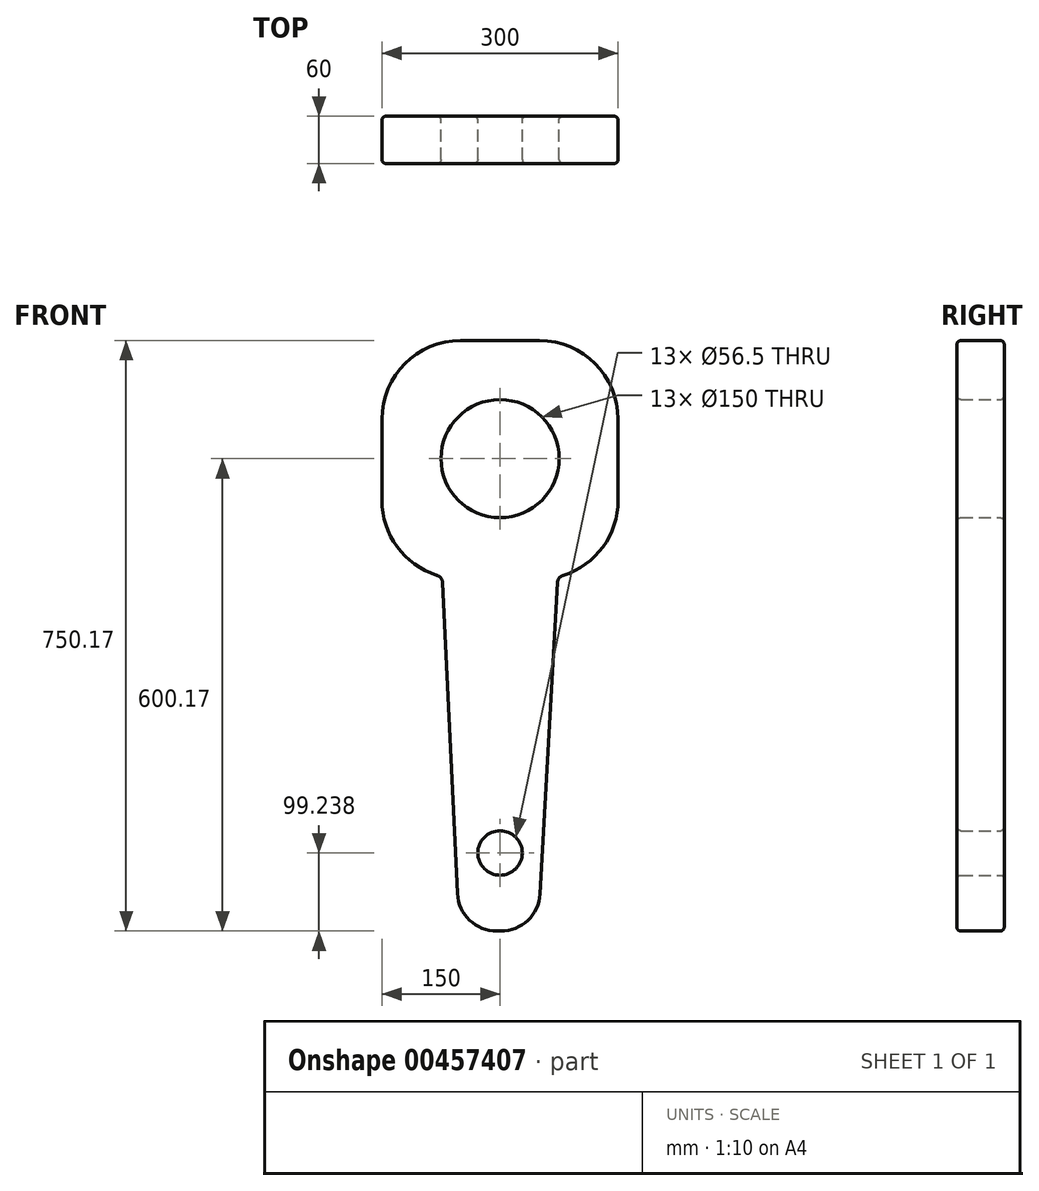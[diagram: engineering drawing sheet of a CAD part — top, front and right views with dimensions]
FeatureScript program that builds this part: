
annotation { "Feature Type Name" : "Feature", "Feature Type Description" : "" }
export const myFeature = defineFeature(function(context is Context, id is Id, definition is map)
    precondition{}
    {
        {
            var Q0;
            Q0=qCreatedBy(makeId("Front.planeOp"),FACE);
            var sketch = newSketch(context, id + "F0", { "sketchPlane" : qUnion([Q0])});
            skLineSegment(sketch, "E0", {"start": v(-51.86, -419.28) * mm, "end": v(48.14, -419.28) * mm});
            skLineSegment(sketch, "E1", {"start": v(150, 330.89) * mm, "end": v(-150, 330.89) * mm});
            skCircle(sketch, "E2", {"center": v(0, -320.04) * mm, "radius": 28.25 * mm});
            skPoint(sketch, "E3", {"position": v(73.4, 30.7) * mm});
            skLineSegment(sketch, "E4", {"start": v(150, 330.89) * mm, "end": v(150, 30.89) * mm});
            skLineSegment(sketch, "E5", {"start": v(150, 30.89) * mm, "end": v(73.4, 30.7) * mm});
            skLineSegment(sketch, "E6", {"start": v(48.14, -419.28) * mm, "end": v(73.4, 30.7) * mm});
            skLineSegment(sketch, "E7", {"start": v(-150, 330.89) * mm, "end": v(-150, 30.89) * mm});
            skLineSegment(sketch, "E8", {"start": v(-150, 30.89) * mm, "end": v(-73.4, 30.89) * mm});
            skLineSegment(sketch, "E9", {"start": v(-73.4, 30.89) * mm, "end": v(-51.86, -419.28) * mm});
            skCircle(sketch, "E10", {"center": v(0, 180.89) * mm, "radius": 75 * mm});
            skSolve(sketch);
        }
        {
            var Q0;
            Q0 = qSketchRegion(id + "F0", true);
            extrude(context, id + "F1", {"entities" : qUnion([Q0]), "depth" : 60 * mm});
        }
        {
            var Q0;
            Q0=makeQuery(id+"F1.opExtrude","SWEPT_EDGE",EDGE,{"disambiguationData":[OSD([sQuery(id+"F0.wireOp",EDGE,"llnWPApp-xlf0-43IF-Cd4r-FyilcEBlqN0B"),sQuery(id+"F0.wireOp",EDGE,"E1")])]});
            var Q1;
            Q1=makeQuery(id+"F1.opExtrude","SWEPT_EDGE",EDGE,{"disambiguationData":[OSD([sQuery(id+"F0.wireOp",EDGE,"E1"),sQuery(id+"F0.wireOp",EDGE,"aOmzhxmz-P9Za-yCZ6-1gEy-kmdqGolYLMVF")])]});
            fillet(context, id + "F2", {"entities" : qUnion([Q0, Q1]), "radius" : 100 * mm, "tangentPropagation" : true, "allowEdgeOverflow" : false});
        }
        {
            var Q0;
            Q0=makeQuery(id+"F1.opExtrude","SWEPT_EDGE",EDGE,{"disambiguationData":[OSD([sQuery(id+"F0.wireOp",EDGE,"E4"),sQuery(id+"F0.wireOp",EDGE,"E5")])]});
            var Q1;
            Q1=makeQuery(id+"F1.opExtrude","SWEPT_EDGE",EDGE,{"disambiguationData":[OSD([sQuery(id+"F0.wireOp",EDGE,"E7"),sQuery(id+"F0.wireOp",EDGE,"E8")])]});
            fillet(context, id + "F3", {"entities" : qUnion([Q0, Q1]), "radius" : 100 * mm, "tangentPropagation" : true, "allowEdgeOverflow" : false});
        }
        {
            var Q0;
            Q0=makeQuery(id+"F3.opFillet","BLEND_EDGE",EDGE,{"blendedFrom":[makeQuery(id+"F1.opExtrude","SWEPT_EDGE",EDGE,{"disambiguationData":[OSD([sQuery(id+"F0.wireOp",EDGE,"E7"),sQuery(id+"F0.wireOp",EDGE,"E8")])]}),makeQuery(id+"F1.opExtrude","SWEPT_FACE",FACE,{"disambiguationData":[OSD([sQuery(id+"F0.wireOp",EDGE,"E9")])]})],"blendedInto":[makeQuery(id+"F1.opExtrude","SWEPT_FACE",FACE,{"disambiguationData":[OSD([sQuery(id+"F0.wireOp",EDGE,"E9")])]})]});
            var Q1;
            Q1=makeQuery(id+"F3.opFillet","BLEND_EDGE",EDGE,{"blendedFrom":[makeQuery(id+"F1.opExtrude","SWEPT_EDGE",EDGE,{"disambiguationData":[OSD([sQuery(id+"F0.wireOp",EDGE,"E4"),sQuery(id+"F0.wireOp",EDGE,"E5")])]}),makeQuery(id+"F1.opExtrude","SWEPT_FACE",FACE,{"disambiguationData":[OSD([sQuery(id+"F0.wireOp",EDGE,"E6")])]})],"blendedInto":[makeQuery(id+"F1.opExtrude","SWEPT_FACE",FACE,{"disambiguationData":[OSD([sQuery(id+"F0.wireOp",EDGE,"E6")])]})]});
            fillet(context, id + "F4", {"entities" : qUnion([Q0, Q1]), "radius" : 10 * mm, "tangentPropagation" : true, "allowEdgeOverflow" : false});
        }
        {
            var Q0;
            Q0=makeQuery(id+"F1.opExtrude","CAP_FACE",FACE,{"disambiguationData":[OSD([sQuery(id+"F0.wireOp",EDGE,"E0"),sQuery(id+"F0.wireOp",EDGE,"E1"),sQuery(id+"F0.wireOp",EDGE,"E2"),sQuery(id+"F0.wireOp",EDGE,"E4"),sQuery(id+"F0.wireOp",EDGE,"E5"),sQuery(id+"F0.wireOp",EDGE,"E6"),sQuery(id+"F0.wireOp",EDGE,"E7"),sQuery(id+"F0.wireOp",EDGE,"E8"),sQuery(id+"F0.wireOp",EDGE,"E9")])],"isStart":true});
            var Q1;
            Q1=makeQuery(id+"F1.opExtrude","CAP_FACE",FACE,{"disambiguationData":[OSD([sQuery(id+"F0.wireOp",EDGE,"E0"),sQuery(id+"F0.wireOp",EDGE,"E1"),sQuery(id+"F0.wireOp",EDGE,"E2"),sQuery(id+"F0.wireOp",EDGE,"E4"),sQuery(id+"F0.wireOp",EDGE,"E5"),sQuery(id+"F0.wireOp",EDGE,"E6"),sQuery(id+"F0.wireOp",EDGE,"E7"),sQuery(id+"F0.wireOp",EDGE,"E8"),sQuery(id+"F0.wireOp",EDGE,"E9")])],"isStart":false});
            fillet(context, id + "F5", {"entities" : qUnion([Q0, Q1]), "radius" : 5 * mm, "tangentPropagation" : true, "allowEdgeOverflow" : false});
        }
        {
            var Q0;
            Q0=makeQuery(id+"F1.opExtrude","SWEPT_EDGE",EDGE,{"disambiguationData":[OSD([sQuery(id+"F0.wireOp",EDGE,"E0"),sQuery(id+"F0.wireOp",EDGE,"E6")])]});
            var Q1;
            Q1=makeQuery(id+"F1.opExtrude","SWEPT_EDGE",EDGE,{"disambiguationData":[OSD([sQuery(id+"F0.wireOp",EDGE,"E0"),sQuery(id+"F0.wireOp",EDGE,"E9")])]});
            fillet(context, id + "F6", {"entities" : qUnion([Q0, Q1]), "radius" : 50 * mm, "tangentPropagation" : true, "allowEdgeOverflow" : false});
        }
    });
